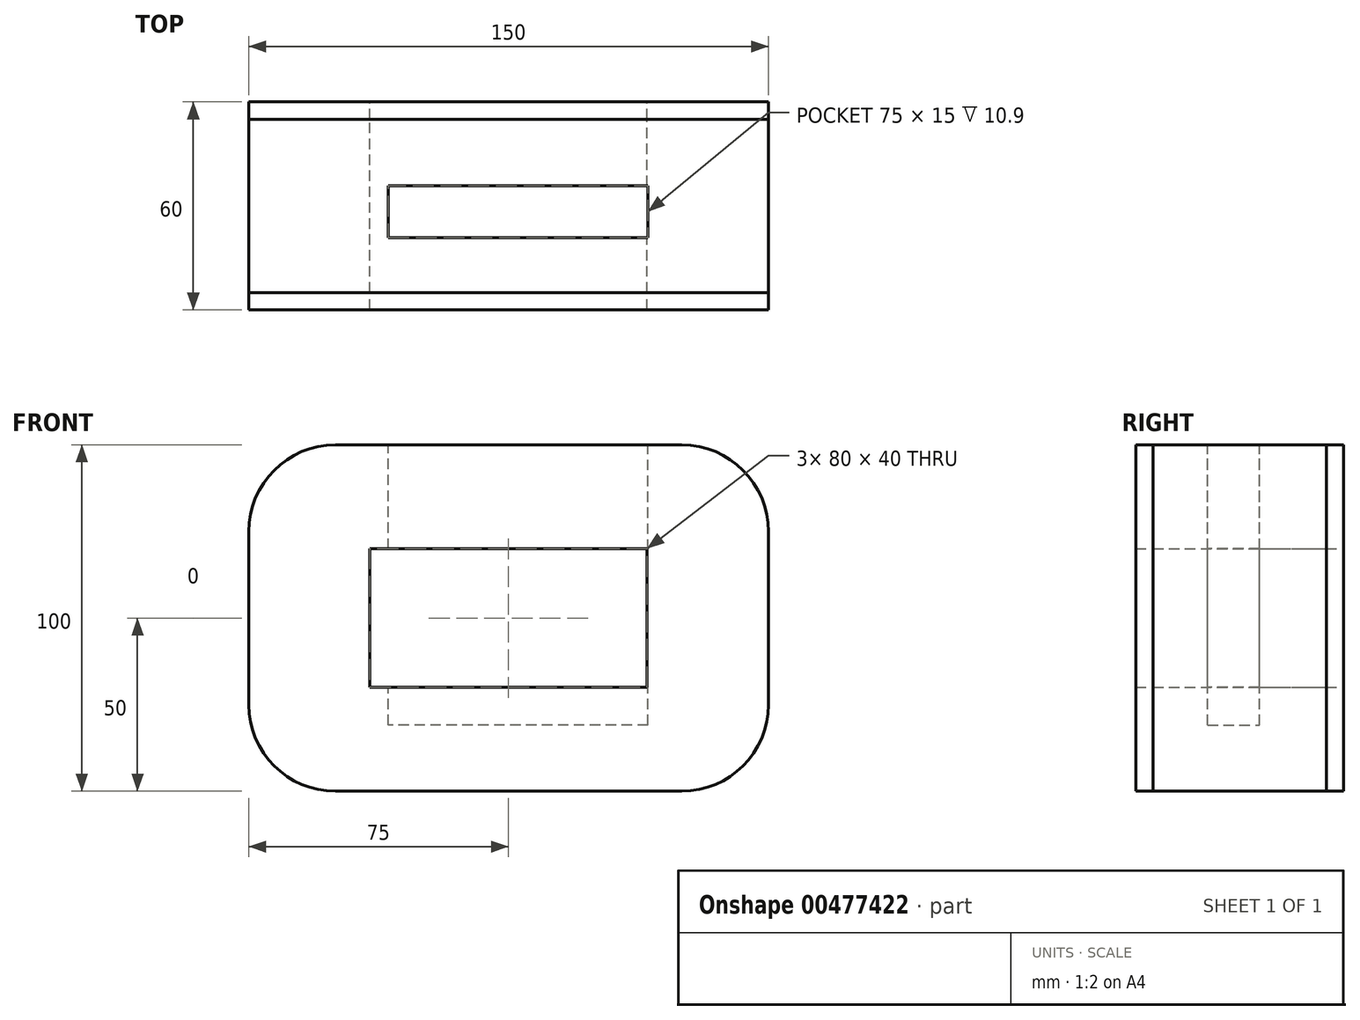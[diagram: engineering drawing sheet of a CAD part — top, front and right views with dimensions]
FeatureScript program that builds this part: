
annotation { "Feature Type Name" : "Feature", "Feature Type Description" : "" }
export const myFeature = defineFeature(function(context is Context, id is Id, definition is map)
    precondition{}
    {
        {
            var Q0;
            Q0=qCreatedBy(makeId("Front.planeOp"),FACE);
            var sketch = newSketch(context, id + "F0", { "sketchPlane" : qUnion([Q0])});
            skLineSegment(sketch, "E0.bottom", {"start": v(-75, 50) * mm, "end": v(75, 50) * mm});
            skLineSegment(sketch, "E0.top", {"start": v(-75, -50) * mm, "end": v(75, -50) * mm});
            skLineSegment(sketch, "E0.left", {"start": v(-75, 50) * mm, "end": v(-75, -50) * mm});
            skLineSegment(sketch, "E0.right", {"start": v(75, 50) * mm, "end": v(75, -50) * mm});
            skPoint(sketch, "E0.middle", {"position": v(0, 0) * mm});
            skSolve(sketch);
        }
        {
            var Q0;
            Q0=makeQuery(id+"F0.imprint","IMPRINT",FACE,{"disambiguationData":[TD([[makeQuery(id+"F0.imprint","IMPRINT",EDGE,{"derivedFrom":sQuery(id+"F0.wireOp",EDGE,"E0.bottom")}),-1.0]])]});
            extrude(context, id + "F1", {"entities" : qUnion([Q0]), "depth" : 50 * mm});
        }
        {
            var Q0;
            Q0=makeQuery(id+"F1.opExtrude","CAP_FACE",FACE,{"disambiguationData":[OSD([sQuery(id+"F0.wireOp",EDGE,"E0.bottom"),sQuery(id+"F0.wireOp",EDGE,"E0.top"),sQuery(id+"F0.wireOp",EDGE,"E0.left"),sQuery(id+"F0.wireOp",EDGE,"E0.right")])],"isStart":false});
            extrude(context, id + "F2", {"entities" : qUnion([Q0]), "depth" : 5 * mm});
        }
        {
            var Q0;
            Q0=makeQuery(id+"F1.opExtrude","CAP_FACE",FACE,{"disambiguationData":[OSD([sQuery(id+"F0.wireOp",EDGE,"E0.bottom"),sQuery(id+"F0.wireOp",EDGE,"E0.top"),sQuery(id+"F0.wireOp",EDGE,"E0.left"),sQuery(id+"F0.wireOp",EDGE,"E0.right")])],"isStart":true});
            var sketch = newSketch(context, id + "F3", { "sketchPlane" : qUnion([Q0])});
            skLineSegment(sketch, "E1.bottom", {"start": v(-40, 20) * mm, "end": v(40, 20) * mm});
            skLineSegment(sketch, "E1.top", {"start": v(-40, -20) * mm, "end": v(40, -20) * mm});
            skLineSegment(sketch, "E1.left", {"start": v(-40, 20) * mm, "end": v(-40, -20) * mm});
            skLineSegment(sketch, "E1.right", {"start": v(40, 20) * mm, "end": v(40, -20) * mm});
            skPoint(sketch, "E1.middle", {"position": v(0, 0) * mm});
            skSolve(sketch);
        }
        {
            var Q0;
            Q0 = qSketchRegion(id + "F3", true);
            extrude(context, id + "F4", {"entities" : qUnion([Q0]), "operationType" : NewBodyOperationType.REMOVE, "oppositeDirection" : true, "depth" : 100 * mm});
        }
        {
            var Q0;
            Q0=makeQuery(id+"F1.opExtrude","CAP_FACE",FACE,{"disambiguationData":[OSD([sQuery(id+"F0.wireOp",EDGE,"E0.bottom"),sQuery(id+"F0.wireOp",EDGE,"E0.top"),sQuery(id+"F0.wireOp",EDGE,"E0.left"),sQuery(id+"F0.wireOp",EDGE,"E0.right")])],"isStart":true});
            var sketch = newSketch(context, id + "F5", { "sketchPlane" : qUnion([Q0])});
            skLineSegment(sketch, "E2.bottom", {"start": v(-75, 50) * mm, "end": v(75, 50) * mm});
            skLineSegment(sketch, "E2.top", {"start": v(-75, -50) * mm, "end": v(75, -50) * mm});
            skLineSegment(sketch, "E2.left", {"start": v(-75, 50) * mm, "end": v(-75, -50) * mm});
            skLineSegment(sketch, "E2.right", {"start": v(75, 50) * mm, "end": v(75, -50) * mm});
            skSolve(sketch);
        }
        {
            var Q0;
            Q0 = qSketchRegion(id + "F5", true);
            extrude(context, id + "F6", {"entities" : qUnion([Q0]), "depth" : 5 * mm});
        }
        {
            var Q0;
            Q0=makeQuery(id+"F6.opExtrude","CAP_FACE",FACE,{"disambiguationData":[OSD([sQuery(id+"F5.wireOp",EDGE,"E2.bottom"),sQuery(id+"F5.wireOp",EDGE,"E2.top"),sQuery(id+"F5.wireOp",EDGE,"E2.left"),sQuery(id+"F5.wireOp",EDGE,"E2.right")])],"isStart":false});
            var sketch = newSketch(context, id + "F7", { "sketchPlane" : qUnion([Q0])});
            skSolve(sketch);
        }
        {
            var Q0;
            Q0=makeQuery(id+"F1.opExtrude","SWEPT_EDGE",EDGE,{"disambiguationData":[OSD([sQuery(id+"F0.wireOp",EDGE,"E0.bottom"),sQuery(id+"F0.wireOp",EDGE,"E0.right")])]});
            fillet(context, id + "F8", {"entities" : qUnion([Q0]), "radius" : 25 * mm, "tangentPropagation" : true, "allowEdgeOverflow" : false});
        }
        {
            var Q0;
            Q0=makeQuery(id+"F1.opExtrude","SWEPT_EDGE",EDGE,{"disambiguationData":[OSD([sQuery(id+"F0.wireOp",EDGE,"E0.bottom"),sQuery(id+"F0.wireOp",EDGE,"E0.left")])]});
            fillet(context, id + "F9", {"entities" : qUnion([Q0]), "radius" : 25 * mm, "tangentPropagation" : true, "allowEdgeOverflow" : false});
        }
        {
            var Q0;
            Q0=makeQuery(id+"F1.opExtrude","SWEPT_EDGE",EDGE,{"disambiguationData":[OSD([sQuery(id+"F0.wireOp",EDGE,"E0.top"),sQuery(id+"F0.wireOp",EDGE,"E0.left")])]});
            fillet(context, id + "F10", {"entities" : qUnion([Q0]), "radius" : 25 * mm, "tangentPropagation" : true, "allowEdgeOverflow" : false});
        }
        {
            var Q0;
            Q0=makeQuery(id+"F1.opExtrude","SWEPT_EDGE",EDGE,{"disambiguationData":[OSD([sQuery(id+"F0.wireOp",EDGE,"E0.top"),sQuery(id+"F0.wireOp",EDGE,"E0.right")])]});
            fillet(context, id + "F11", {"entities" : qUnion([Q0]), "radius" : 25 * mm, "tangentPropagation" : true, "allowEdgeOverflow" : false});
        }
        {
            var Q0;
            Q0=makeQuery(id+"F2.opExtrude","SWEPT_EDGE",EDGE,{"disambiguationData":[OSD([sQuery(id+"F0.wireOp",EDGE,"E0.bottom"),sQuery(id+"F0.wireOp",EDGE,"E0.left")])]});
            fillet(context, id + "F12", {"entities" : qUnion([Q0]), "radius" : 25 * mm, "tangentPropagation" : true, "allowEdgeOverflow" : false});
        }
        {
            var Q0;
            Q0=makeQuery(id+"F2.opExtrude","SWEPT_EDGE",EDGE,{"disambiguationData":[OSD([sQuery(id+"F0.wireOp",EDGE,"E0.bottom"),sQuery(id+"F0.wireOp",EDGE,"E0.right")])]});
            fillet(context, id + "F13", {"entities" : qUnion([Q0]), "radius" : 25 * mm, "tangentPropagation" : true, "allowEdgeOverflow" : false});
        }
        {
            var Q0;
            Q0=makeQuery(id+"F2.opExtrude","SWEPT_EDGE",EDGE,{"disambiguationData":[OSD([sQuery(id+"F0.wireOp",EDGE,"E0.top"),sQuery(id+"F0.wireOp",EDGE,"E0.left")])]});
            fillet(context, id + "F14", {"entities" : qUnion([Q0]), "radius" : 25 * mm, "tangentPropagation" : true, "allowEdgeOverflow" : false});
        }
        {
            var Q0;
            Q0=makeQuery(id+"F2.opExtrude","SWEPT_EDGE",EDGE,{"disambiguationData":[OSD([sQuery(id+"F0.wireOp",EDGE,"E0.top"),sQuery(id+"F0.wireOp",EDGE,"E0.right")])]});
            fillet(context, id + "F15", {"entities" : qUnion([Q0]), "radius" : 25 * mm, "tangentPropagation" : true, "allowEdgeOverflow" : false});
        }
        {
            var Q0;
            Q0=makeQuery(id+"F6.opExtrude","SWEPT_EDGE",EDGE,{"disambiguationData":[OSD([sQuery(id+"F5.wireOp",EDGE,"E2.bottom"),sQuery(id+"F5.wireOp",EDGE,"E2.right")])]});
            fillet(context, id + "F16", {"entities" : qUnion([Q0]), "radius" : 25 * mm, "tangentPropagation" : true, "allowEdgeOverflow" : false});
        }
        {
            var Q0;
            Q0=makeQuery(id+"F6.opExtrude","SWEPT_EDGE",EDGE,{"disambiguationData":[OSD([sQuery(id+"F5.wireOp",EDGE,"E2.top"),sQuery(id+"F5.wireOp",EDGE,"E2.right")])]});
            fillet(context, id + "F17", {"entities" : qUnion([Q0]), "radius" : 25 * mm, "tangentPropagation" : true, "allowEdgeOverflow" : false});
        }
        {
            var Q0;
            Q0=makeQuery(id+"F6.opExtrude","SWEPT_EDGE",EDGE,{"disambiguationData":[OSD([sQuery(id+"F5.wireOp",EDGE,"E2.bottom"),sQuery(id+"F5.wireOp",EDGE,"E2.left")])]});
            fillet(context, id + "F18", {"entities" : qUnion([Q0]), "radius" : 25 * mm, "tangentPropagation" : true, "allowEdgeOverflow" : false});
        }
        {
            var Q0;
            Q0=makeQuery(id+"F6.opExtrude","SWEPT_EDGE",EDGE,{"disambiguationData":[OSD([sQuery(id+"F5.wireOp",EDGE,"E2.top"),sQuery(id+"F5.wireOp",EDGE,"E2.left")])]});
            fillet(context, id + "F19", {"entities" : qUnion([Q0]), "radius" : 25 * mm, "tangentPropagation" : true, "allowEdgeOverflow" : false});
        }
        {
            var Q0;
            Q0=makeQuery(id+"F7.imprint","IMPRINT",FACE,{"disambiguationData":[TD([[makeQuery(id+"F7.imprint","IMPRINT",EDGE,{"derivedFrom":makeQuery(id+"F6.opExtrude","CAP_EDGE",EDGE,{"disambiguationData":[OSD([sQuery(id+"F5.wireOp",EDGE,"E2.bottom")])],"isStart":false})}),1.0]])]});
            var sketch = newSketch(context, id + "F20", { "sketchPlane" : qUnion([Q0])});
            skLineSegment(sketch, "E3.bottom", {"start": v(-40, 20) * mm, "end": v(40, 20) * mm});
            skLineSegment(sketch, "E3.top", {"start": v(-40, -20) * mm, "end": v(40, -20) * mm});
            skLineSegment(sketch, "E3.left", {"start": v(-40, 20) * mm, "end": v(-40, -20) * mm});
            skLineSegment(sketch, "E3.right", {"start": v(40, 20) * mm, "end": v(40, -20) * mm});
            skPoint(sketch, "E3.middle", {"position": v(0, 0) * mm});
            skSolve(sketch);
        }
        {
            var Q0;
            Q0 = qSketchRegion(id + "F20", true);
            extrude(context, id + "F21", {"entities" : qUnion([Q0]), "operationType" : NewBodyOperationType.REMOVE, "oppositeDirection" : true, "depth" : 100 * mm});
        }
        {
            var Q0;
            Q0=makeQuery(id+"F1.opExtrude","SWEPT_FACE",FACE,{"disambiguationData":[OSD([sQuery(id+"F0.wireOp",EDGE,"E0.bottom")])]});
            var sketch = newSketch(context, id + "F22", { "sketchPlane" : qUnion([Q0])});
            skLineSegment(sketch, "E4.bottom", {"start": v(40.24, -34.25) * mm, "end": v(-34.76, -34.25) * mm});
            skLineSegment(sketch, "E4.top", {"start": v(40.24, -19.25) * mm, "end": v(-34.76, -19.25) * mm});
            skLineSegment(sketch, "E4.left", {"start": v(40.24, -34.25) * mm, "end": v(40.24, -19.25) * mm});
            skLineSegment(sketch, "E4.right", {"start": v(-34.76, -34.25) * mm, "end": v(-34.76, -19.25) * mm});
            skPoint(sketch, "E4.middle", {"position": v(2.74, -26.75) * mm});
            skSolve(sketch);
        }
        {
            var Q0;
            Q0 = qSketchRegion(id + "F22", true);
            extrude(context, id + "F23", {"entities" : qUnion([Q0]), "operationType" : NewBodyOperationType.REMOVE, "oppositeDirection" : true, "depth" : 80.9 * mm});
        }
    });
